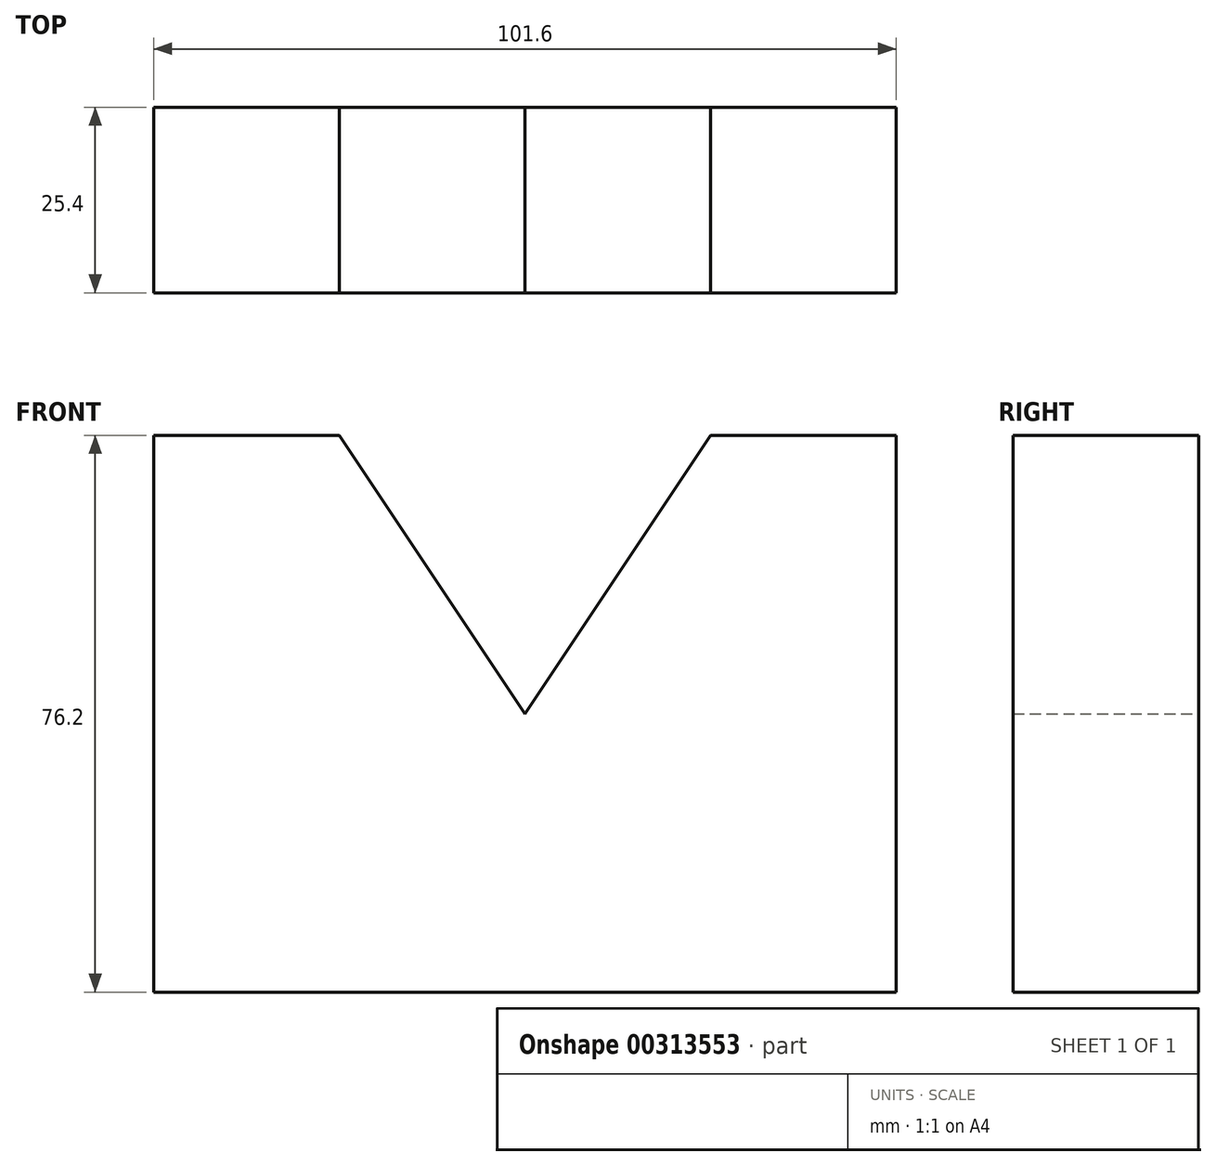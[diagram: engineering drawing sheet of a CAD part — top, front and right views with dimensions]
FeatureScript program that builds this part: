
annotation { "Feature Type Name" : "Feature", "Feature Type Description" : "" }
export const myFeature = defineFeature(function(context is Context, id is Id, definition is map)
    precondition{}
    {
        {
            var Q0;
            Q0=qCreatedBy(makeId("Front.planeOp"),FACE);
            var sketch = newSketch(context, id + "F0", { "sketchPlane" : qUnion([Q0])});
            skLineSegment(sketch, "E0", {"start": v(41.27, -23.36) * mm, "end": v(-60.33, -23.36) * mm});
            skLineSegment(sketch, "E1", {"start": v(41.27, -23.36) * mm, "end": v(41.27, 52.84) * mm});
            skLineSegment(sketch, "E2", {"start": v(-60.33, -23.36) * mm, "end": v(-60.33, 52.84) * mm});
            skLineSegment(sketch, "E3", {"start": v(-60.33, 52.84) * mm, "end": v(-34.93, 52.84) * mm});
            skLineSegment(sketch, "E4", {"start": v(41.27, 52.84) * mm, "end": v(15.87, 52.84) * mm});
            skLineSegment(sketch, "E5", {"start": v(-34.93, 52.84) * mm, "end": v(-9.53, 14.74) * mm});
            skLineSegment(sketch, "E6", {"start": v(15.87, 52.84) * mm, "end": v(-9.53, 14.74) * mm});
            skSolve(sketch);
        }
        {
            var Q0;
            Q0=makeQuery(id+"F0.imprint","IMPRINT",FACE,{"disambiguationData":[TD([[makeQuery(id+"F0.imprint","IMPRINT",EDGE,{"derivedFrom":sQuery(id+"F0.wireOp",EDGE,"E0")}),-1.0]])]});
            extrude(context, id + "F1", {"entities" : qUnion([Q0]), "depth" : 25.4 * mm});
        }
    });
